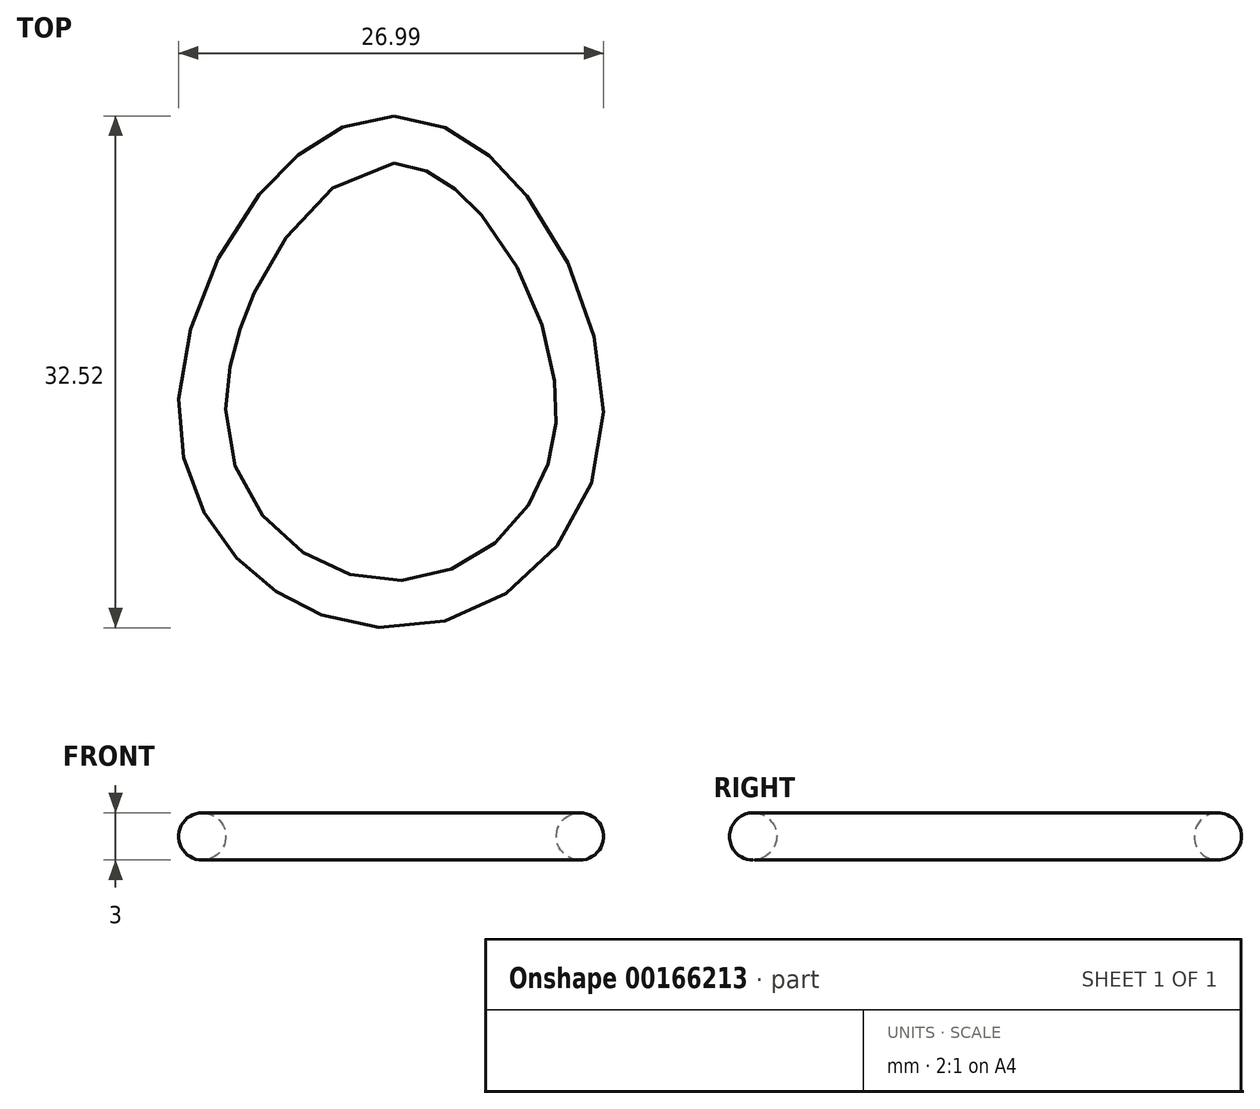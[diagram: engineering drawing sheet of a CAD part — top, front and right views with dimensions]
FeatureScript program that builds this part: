
annotation { "Feature Type Name" : "Feature", "Feature Type Description" : "" }
export const myFeature = defineFeature(function(context is Context, id is Id, definition is map)
    precondition{}
    {
        {
            var Q0;
            Q0=qCreatedBy(makeId("Top.planeOp"),FACE);
            var sketch = newSketch(context, id + "F0", { "sketchPlane" : qUnion([Q0])});
            skFitSpline(sketch, "E0", {"points": [v(0, -11.3) * mm, v(-12.14, 0) * mm, v(0, 18.22) * mm, v(11.77, 0) * mm, v(0, -11.3) * mm]});
            skSolve(sketch);
        }
        {
            var Q0;
            Q0=qCreatedBy(makeId("Right.planeOp"),FACE);
            var sketch = newSketch(context, id + "F1", { "sketchPlane" : qUnion([Q0])});
            skPoint(sketch, "E1.0", {"position": v(0, 0) * mm});
            skPoint(sketch, "E2.0", {"position": v(18.22, 0) * mm});
            skCircle(sketch, "E3", {"center": v(18.22, 0) * mm, "radius": 1.5 * mm});
            skSolve(sketch);
        }
        {
            var Q0;
            Q0=makeQuery(id+"F1.imprint","IMPRINT",FACE,{"disambiguationData":[TD([[makeQuery(id+"F1.imprint","IMPRINT",EDGE,{"derivedFrom":sQuery(id+"F1.wireOp",EDGE,"E3")}),1.0]])]});
            var Q1;
            Q1=sQuery(id+"F0.wireOp",EDGE,"E0");
            sweep(context, id + "F2", {"profiles" : qUnion([Q0]), "path" : qUnion([Q1])});
        }
    });
